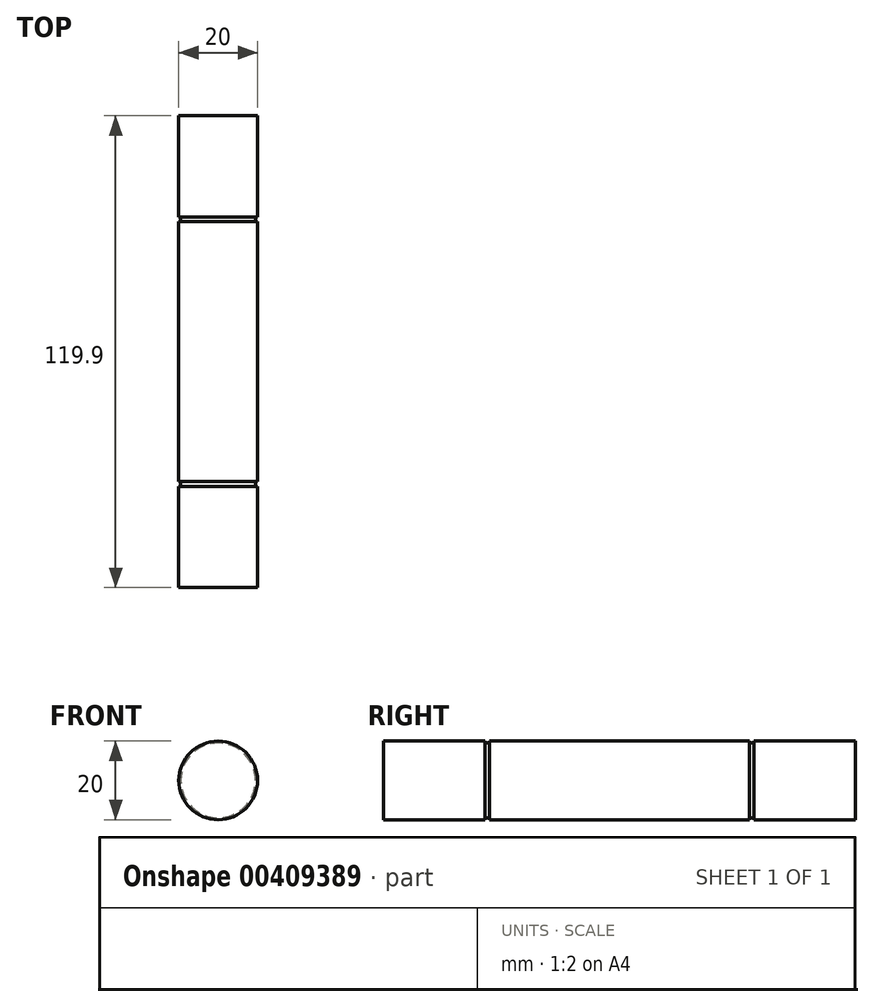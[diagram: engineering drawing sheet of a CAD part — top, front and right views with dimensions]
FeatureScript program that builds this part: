
annotation { "Feature Type Name" : "Feature", "Feature Type Description" : "" }
export const myFeature = defineFeature(function(context is Context, id is Id, definition is map)
    precondition{}
    {
        {
            var Q0;
            Q0=qCreatedBy(makeId("Right.planeOp"),FACE);
            var sketch = newSketch(context, id + "F0", { "sketchPlane" : qUnion([Q0])});
            skLineSegment(sketch, "E0", {"start": v(0, 0) * mm, "end": v(0, 10) * mm});
            skLineSegment(sketch, "E1", {"start": v(0, 10) * mm, "end": v(25.75, 10) * mm});
            skLineSegment(sketch, "E2", {"start": v(25.75, 10) * mm, "end": v(25.75, 9.5) * mm});
            skLineSegment(sketch, "E3", {"start": v(25.75, 9.5) * mm, "end": v(26.95, 9.5) * mm});
            skLineSegment(sketch, "E4", {"start": v(26.95, 9.5) * mm, "end": v(26.95, 10) * mm});
            skLineSegment(sketch, "E5", {"start": v(26.95, 10) * mm, "end": v(92.95, 10) * mm});
            skLineSegment(sketch, "E6", {"start": v(92.95, 10) * mm, "end": v(92.95, 9.5) * mm});
            skLineSegment(sketch, "E7", {"start": v(92.95, 9.5) * mm, "end": v(94.15, 9.5) * mm});
            skLineSegment(sketch, "E8", {"start": v(94.15, 9.5) * mm, "end": v(94.15, 10) * mm});
            skLineSegment(sketch, "E9", {"start": v(94.15, 10) * mm, "end": v(119.9, 10) * mm});
            skLineSegment(sketch, "E10", {"start": v(119.9, 10) * mm, "end": v(119.9, 0) * mm});
            skLineSegment(sketch, "E11", {"start": v(119.9, 0) * mm, "end": v(0, 0) * mm});
            skSolve(sketch);
        }
        {
            var Q0;
            Q0=makeQuery(id+"F0.imprint","IMPRINT",FACE,{"disambiguationData":[TD([[makeQuery(id+"F0.imprint","IMPRINT",EDGE,{"derivedFrom":sQuery(id+"F0.wireOp",EDGE,"E0")}),-1.0]])]});
            var Q1;
            Q1=sQuery(id+"F0.wireOp",EDGE,"E11");
            revolve(context, id + "F1", {"entities" : qUnion([Q0]), "axis" : qUnion([Q1]), "revolveType" : RevolveType.FULL});
        }
    });
